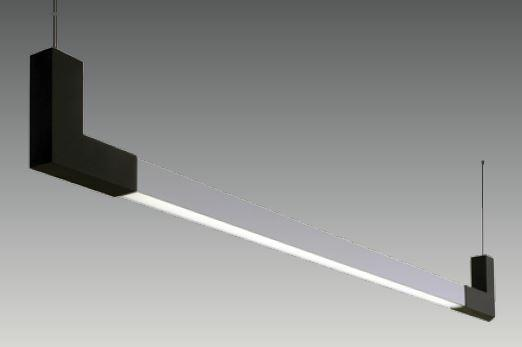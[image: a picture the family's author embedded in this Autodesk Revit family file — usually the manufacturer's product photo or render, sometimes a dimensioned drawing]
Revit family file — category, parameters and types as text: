
# Revit family: SD 1500 PLU
name_source: partatom
category: Lighting Fixtures
revit_build: Autodesk Revit 2017 (Build: 20160225_1515(x64)
units: mm (PartAtom-declared; Revit-internal decimal feet)

## family parameters
Cut with Voids When Loaded = No
Host = Face
Light Source = Yes
Part Type = Normal
Room Calculation Point = No
Round Connector Dimension = Use Diameter
Shared = No

## types (2) — shared parameters
Color Filter = 16777215
Default Elevation = 1219 mm
Dimming Lamp Color Temperature Shift = <None>
Emit Shape Visible in Rendering = Yes
Emit from Rectangle Length = 40 mm  [stored 0.131234 ft]
Emit from Rectangle Width = 1140 mm  [stored 3.74016 ft]
Light Source Symbol Size = 610 mm
Manufacturer = ARLIGHT
Type Image = SD 1500 PLU.JPG
Wattage Comments = 44W

## type names (no varying parameters)
- SDPLU.1500.44.30
- SDPLU.1500.44.40

note: [stored X ft] marks values corroborated as IEEE doubles in the binary element streams (Revit-internal decimal feet)

## geometry (parser evidence)
native form markers: Sweep x3
no freeform markers — native parametric forms only
